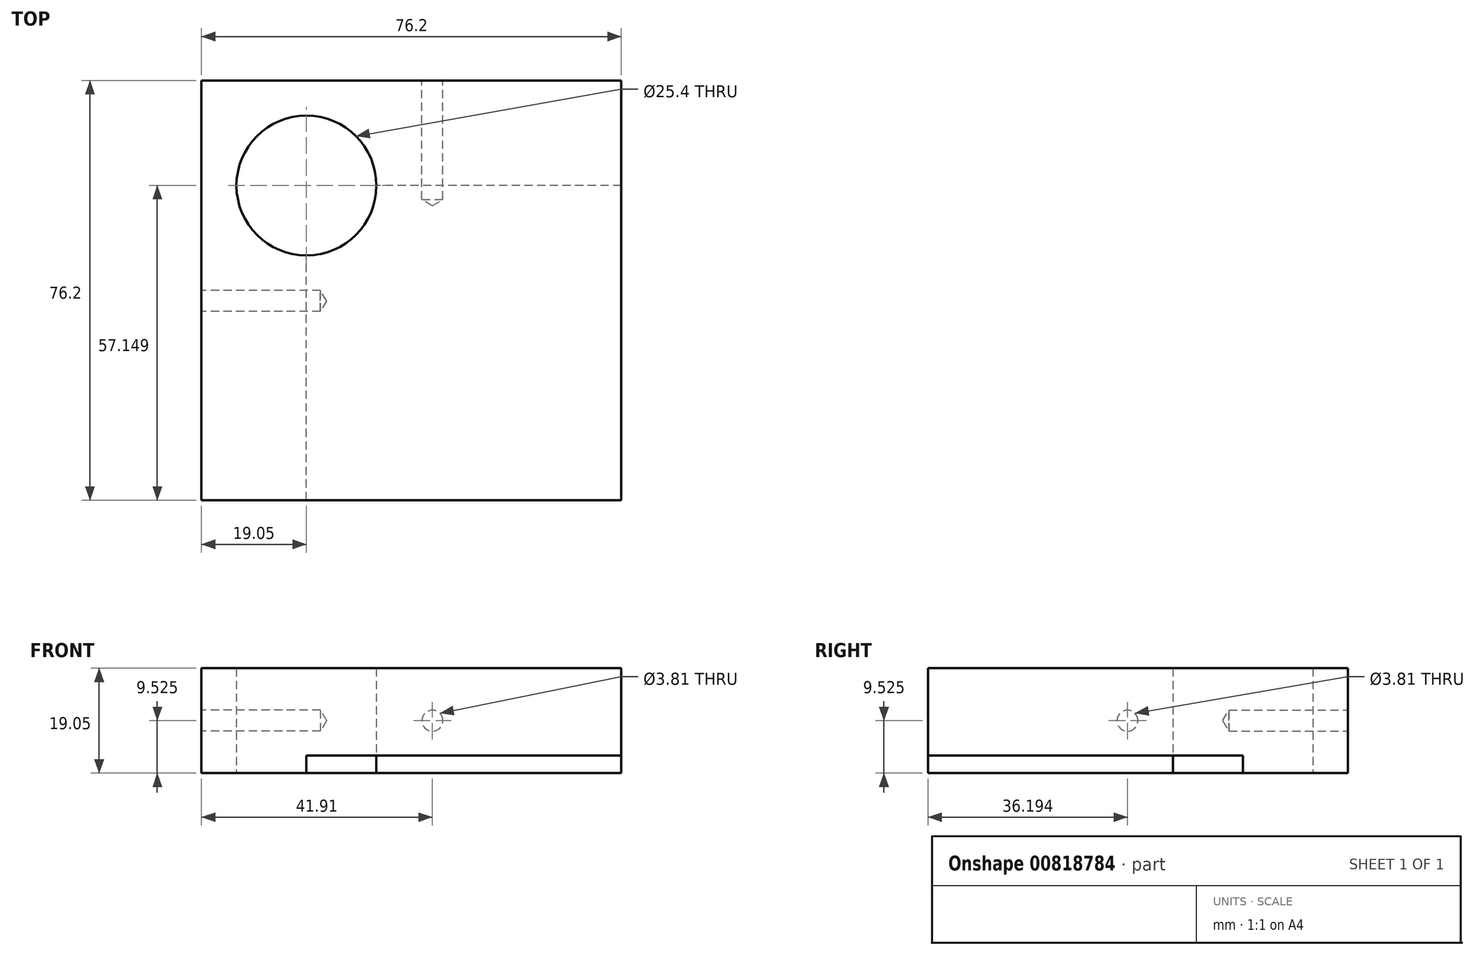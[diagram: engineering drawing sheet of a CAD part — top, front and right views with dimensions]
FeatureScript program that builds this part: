
annotation { "Feature Type Name" : "Feature", "Feature Type Description" : "" }
export const myFeature = defineFeature(function(context is Context, id is Id, definition is map)
    precondition{}
    {
        {
            var Q0;
            Q0=qCreatedBy(makeId("Top.planeOp"),FACE);
            var sketch = newSketch(context, id + "F0", { "sketchPlane" : qUnion([Q0])});
            skLineSegment(sketch, "E0.top", {"start": v(38.1, 33.9) * mm, "end": v(-38.1, 33.9) * mm});
            skPoint(sketch, "E0.middle", {"position": v(0, 0) * mm});
            skLineSegment(sketch, "E1.1", {"start": v(-19.05, -42.3) * mm, "end": v(-19.05, 14.86) * mm});
            skLineSegment(sketch, "E2.0", {"start": v(38.1, 14.86) * mm, "end": v(-19.05, 14.86) * mm});
            skCircle(sketch, "E3", {"center": v(-19.05, 14.86) * mm, "radius": 12.7 * mm});
            skLineSegment(sketch, "E4", {"start": v(-38.1, 33.9) * mm, "end": v(-38.1, -42.3) * mm});
            skLineSegment(sketch, "E5", {"start": v(-38.1, -42.3) * mm, "end": v(38.1, -42.3) * mm});
            skLineSegment(sketch, "E6", {"start": v(38.1, -42.3) * mm, "end": v(38.1, 33.9) * mm});
            skSolve(sketch);
        }
        {
            var Q0;
            {var subQ0=sQuery(id+"F0.wireOp",EDGE,"E5");var subQ1=sQuery(id+"F0.wireOp",EDGE,"E1.1");var subQ2=makeQuery(id+"F0.imprint","INTERSECT",VERTEX,{"derivedFrom":[subQ1,subQ0]});Q0=makeQuery(id+"F0.imprint","IMPRINT",FACE,{"disambiguationData":[TD([[makeQuery(id+"F0.imprint","IMPRINT",EDGE,{"disambiguationData":[TD([[subQ2,-1.0]])],"derivedFrom":subQ1}),-1.0]])]});}
            var Q1;
            {var subQ9=sQuery(id+"F0.wireOp",EDGE,"E0.top");Q1=makeQuery(id+"F0.imprint","IMPRINT",FACE,{"disambiguationData":[TD([[makeQuery(id+"F0.imprint","IMPRINT",EDGE,{"derivedFrom":subQ9}),1.0]])]});}
            extrude(context, id + "F1", {"entities" : qUnion([Q0, Q1]), "depth" : 19.05 * mm, "offsetDistance" : 25.4 * mm});
        }
        {
            var Q0;
            {var subQ0=sQuery(id+"F0.wireOp",EDGE,"E5");var subQ1=sQuery(id+"F0.wireOp",EDGE,"E1.1");var subQ2=makeQuery(id+"F0.imprint","INTERSECT",VERTEX,{"derivedFrom":[subQ1,subQ0]});Q0=makeQuery(id+"F0.imprint","IMPRINT",FACE,{"disambiguationData":[TD([[makeQuery(id+"F0.imprint","IMPRINT",EDGE,{"disambiguationData":[TD([[subQ2,-1.0]])],"derivedFrom":subQ1}),-1.0]])]});}
            extrude(context, id + "F2", {"entities" : qUnion([Q0]), "operationType" : NewBodyOperationType.REMOVE, "depth" : 3.17 * mm, "offsetDistance" : 25.4 * mm});
        }
        {
            var Q0;
            Q0=makeQuery(id+"F1.opExtrude","SWEPT_FACE",FACE,{"disambiguationData":[OSD([sQuery(id+"F0.wireOp",EDGE,"E4")])]});
            var sketch = newSketch(context, id + "F3", { "sketchPlane" : qUnion([Q0])});
            skLineSegment(sketch, "E7.0.0", {"start": v(-33.9, 0) * mm, "end": v(42.3, 0) * mm});
            skLineSegment(sketch, "E7.0.1", {"start": v(42.3, 0) * mm, "end": v(42.3, 19.05) * mm});
            skLineSegment(sketch, "E7.0.2", {"start": v(42.3, 19.05) * mm, "end": v(-33.9, 19.05) * mm});
            skLineSegment(sketch, "E7.0.3", {"start": v(-33.9, 19.05) * mm, "end": v(-33.9, 0) * mm});
            skCircle(sketch, "E8", {"center": v(6.1, 9.53) * mm, "radius": 1.9 * mm});
            skSolve(sketch);
        }
        {
            var Q0;
            Q0=sQuery(id+"F3.wireOp",VERTEX,"E8.center");
            var Q1;
            Q1=makeQuery(id+"F1.opExtrude","SWEPT_BODY",BODY,{"disambiguationData":[OSD([sQuery(id+"F0.wireOp",EDGE,"E0.top"),sQuery(id+"F0.wireOp",EDGE,"E3"),sQuery(id+"F0.wireOp",EDGE,"E4"),sQuery(id+"F0.wireOp",EDGE,"E5"),sQuery(id+"F0.wireOp",EDGE,"E6")])]});
            hole(context, id + "F4", {"style" : HoleStyle.SIMPLE, "endStyle" : HoleEndStyle.BLIND, "holeDiameter" : 3.8 * mm, "majorDiameter" : 6.35 * mm, "holeDepth" : 21.59 * mm, "isTappedThrough" : true, "tappedDepth" : 12.7 * mm, "tapClearance" : 3, "locations" : qUnion([Q0]), "scope" : qUnion([Q1])});
        }
        {
            var Q0;
            Q0=makeQuery(id+"F1.opExtrude","SWEPT_FACE",FACE,{"disambiguationData":[OSD([sQuery(id+"F0.wireOp",EDGE,"E0.top")])]});
            var sketch = newSketch(context, id + "F5", { "sketchPlane" : qUnion([Q0])});
            skLineSegment(sketch, "E9.0.0", {"start": v(-38.1, 0) * mm, "end": v(38.1, 0) * mm});
            skLineSegment(sketch, "E9.0.1", {"start": v(38.1, 0) * mm, "end": v(38.1, 19.05) * mm});
            skLineSegment(sketch, "E9.0.2", {"start": v(38.1, 19.05) * mm, "end": v(-38.1, 19.05) * mm});
            skLineSegment(sketch, "E9.0.3", {"start": v(-38.1, 19.05) * mm, "end": v(-38.1, 0) * mm});
            skLineSegment(sketch, "E10.0", {"start": v(38.1, 9.53) * mm, "end": v(-38.1, 9.53) * mm});
            skLineSegment(sketch, "E11.0", {"start": v(-3.8, 0) * mm, "end": v(-3.8, 19.05) * mm});
            skCircle(sketch, "E12", {"center": v(-3.8, 9.53) * mm, "radius": 1.9 * mm});
            skSolve(sketch);
        }
        {
            var Q0;
            Q0=sQuery(id+"F5.wireOp",VERTEX,"E12.center");
            var Q1;
            Q1=makeQuery(id+"F1.opExtrude","SWEPT_BODY",BODY,{"disambiguationData":[OSD([sQuery(id+"F0.wireOp",EDGE,"E0.top"),sQuery(id+"F0.wireOp",EDGE,"E3"),sQuery(id+"F0.wireOp",EDGE,"E4"),sQuery(id+"F0.wireOp",EDGE,"E5"),sQuery(id+"F0.wireOp",EDGE,"E6")])]});
            hole(context, id + "F6", {"style" : HoleStyle.SIMPLE, "endStyle" : HoleEndStyle.BLIND, "holeDiameter" : 3.8 * mm, "majorDiameter" : 6.35 * mm, "holeDepth" : 21.59 * mm, "isTappedThrough" : true, "tappedDepth" : 12.7 * mm, "tapClearance" : 3, "startFromSketch" : true, "locations" : qUnion([Q0]), "scope" : qUnion([Q1])});
        }
    });
